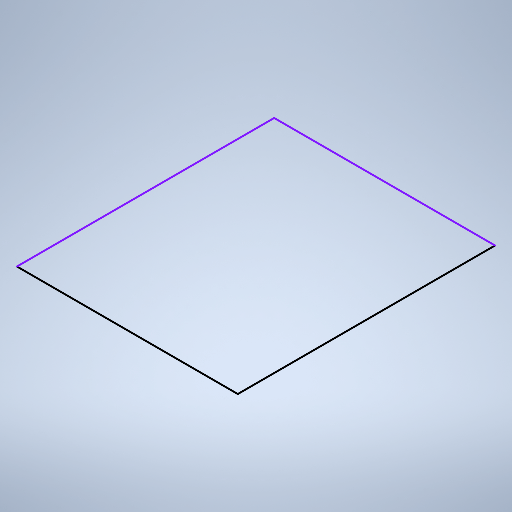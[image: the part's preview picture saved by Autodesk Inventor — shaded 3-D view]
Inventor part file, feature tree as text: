
AUTODESK INVENTOR PART (.ipt)
format: ipt  version: 2025.1 (Build 291241020, 241B)  size: 230,912 bytes
history: native  units: in
note: dims shown in document units (in); Inventor stores cm internally (conversion verified against a paired STEP export)
features: sketch x1
ambient origin geometry x8: Origin, YZ Plane, XZ Plane, XY Plane, X Axis, Y Axis, Z Axis, Center Point
feature tree (1):
  sketch  "Sketch2"
